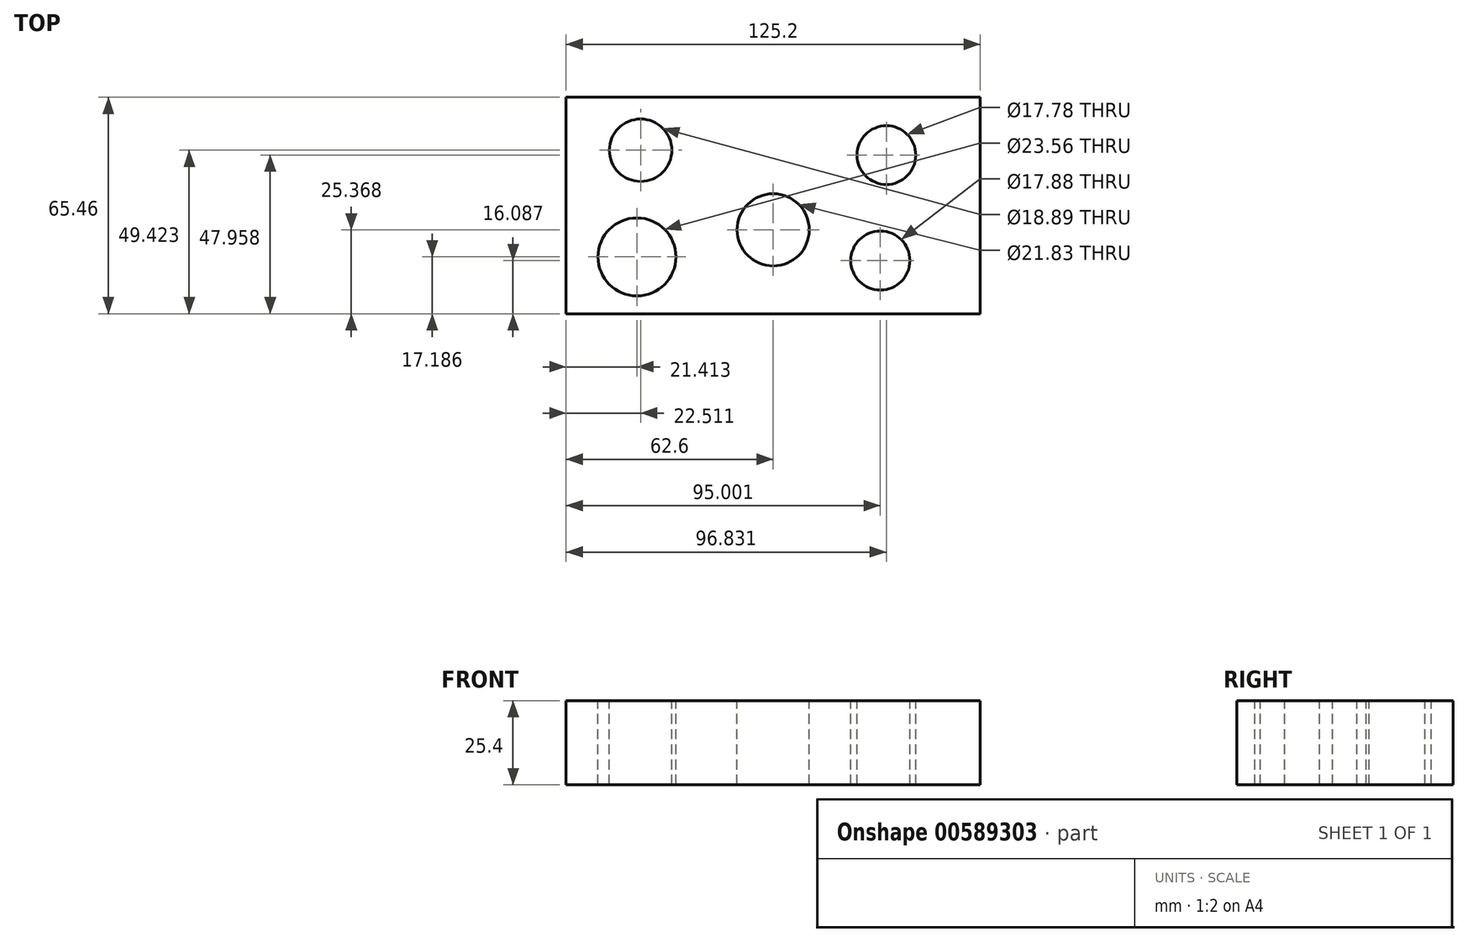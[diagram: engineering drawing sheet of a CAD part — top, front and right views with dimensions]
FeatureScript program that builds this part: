
annotation { "Feature Type Name" : "Feature", "Feature Type Description" : "" }
export const myFeature = defineFeature(function(context is Context, id is Id, definition is map)
    precondition{}
    {
        {
            var Q0;
            Q0=qCreatedBy(makeId("Top.planeOp"),FACE);
            var sketch = newSketch(context, id + "F0", { "sketchPlane" : qUnion([Q0])});
            skLineSegment(sketch, "E0.bottom", {"start": v(62.6, -32.73) * mm, "end": v(-62.6, -32.73) * mm});
            skLineSegment(sketch, "E0.top", {"start": v(62.6, 32.73) * mm, "end": v(-62.6, 32.73) * mm});
            skLineSegment(sketch, "E0.left", {"start": v(62.6, -32.73) * mm, "end": v(62.6, 32.73) * mm});
            skLineSegment(sketch, "E0.right", {"start": v(-62.6, -32.73) * mm, "end": v(-62.6, 32.73) * mm});
            skPoint(sketch, "E0.middle", {"position": v(0, 0) * mm});
            skSolve(sketch);
        }
        {
            var Q0;
            Q0 = qSketchRegion(id + "F0", true);
            extrude(context, id + "F1", {"entities" : qUnion([Q0]), "depth" : 25.4 * mm, "offsetDistance" : 25.4 * mm});
        }
        {
            var Q0;
            Q0=makeQuery(id+"F1.opExtrude","CAP_FACE",FACE,{"disambiguationData":[OSD([sQuery(id+"F0.wireOp",EDGE,"E0.bottom"),sQuery(id+"F0.wireOp",EDGE,"E0.top"),sQuery(id+"F0.wireOp",EDGE,"E0.left"),sQuery(id+"F0.wireOp",EDGE,"E0.right")])],"isStart":false});
            var sketch = newSketch(context, id + "F2", { "sketchPlane" : qUnion([Q0])});
            skCircle(sketch, "E1", {"center": v(34.23, 15.23) * mm, "radius": 8.89 * mm});
            skCircle(sketch, "E2", {"center": v(-40.09, 16.7) * mm, "radius": 9.45 * mm});
            skCircle(sketch, "E3", {"center": v(32.4, -16.64) * mm, "radius": 8.94 * mm});
            skCircle(sketch, "E4", {"center": v(-41.19, -15.54) * mm, "radius": 11.78 * mm});
            skSolve(sketch);
        }
        {
            var Q0;
            Q0 = qSketchRegion(id + "F2", true);
            extrude(context, id + "F3", {"entities" : qUnion([Q0]), "operationType" : NewBodyOperationType.REMOVE, "oppositeDirection" : true, "depth" : 25.4 * mm, "offsetDistance" : 25.4 * mm});
        }
        {
            var Q0;
            Q0=makeQuery(id+"F1.opExtrude","CAP_FACE",FACE,{"disambiguationData":[OSD([sQuery(id+"F0.wireOp",EDGE,"E0.bottom"),sQuery(id+"F0.wireOp",EDGE,"E0.top"),sQuery(id+"F0.wireOp",EDGE,"E0.left"),sQuery(id+"F0.wireOp",EDGE,"E0.right")])],"isStart":false});
            var sketch = newSketch(context, id + "F4", { "sketchPlane" : qUnion([Q0])});
            skCircle(sketch, "E5", {"center": v(0, -7.36) * mm, "radius": 10.91 * mm});
            skSolve(sketch);
        }
        {
            var Q0;
            Q0=makeQuery(id+"F4.imprint","IMPRINT",FACE,{"disambiguationData":[TD([[makeQuery(id+"F4.imprint","IMPRINT",EDGE,{"derivedFrom":sQuery(id+"F4.wireOp",EDGE,"E5")}),1.0]])]});
            extrude(context, id + "F5", {"entities" : qUnion([Q0]), "operationType" : NewBodyOperationType.REMOVE, "oppositeDirection" : true, "depth" : 25.4 * mm, "offsetDistance" : 25.4 * mm, "hasSecondDirection" : true, "secondDirectionOppositeDirection" : false, "secondDirectionDepth" : 25.4 * mm});
        }
    });
